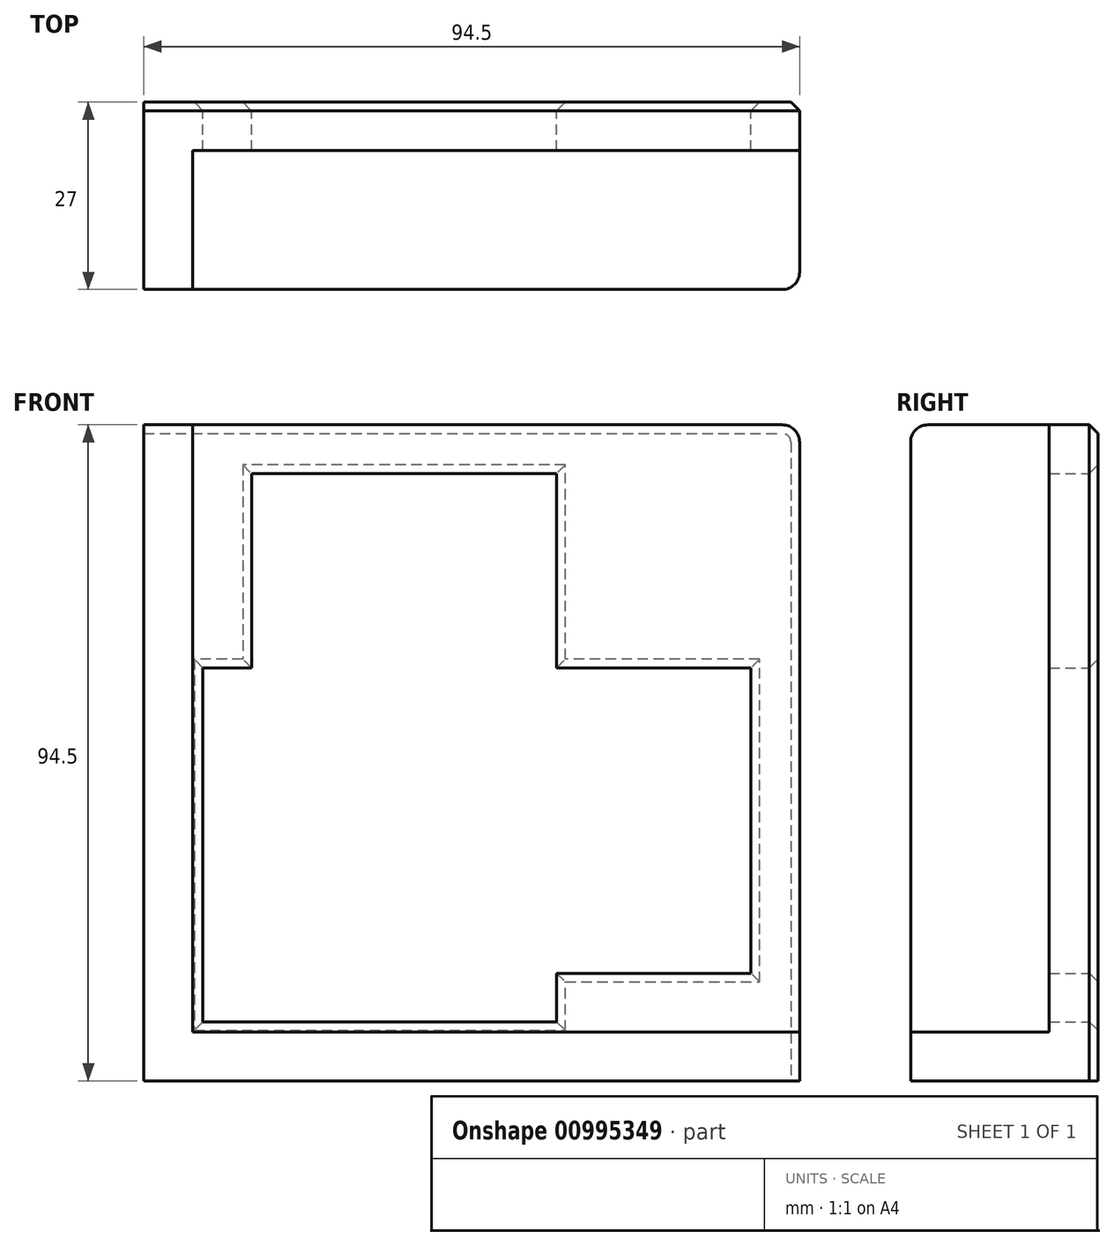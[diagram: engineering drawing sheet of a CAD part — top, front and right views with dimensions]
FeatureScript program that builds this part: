
annotation { "Feature Type Name" : "Feature", "Feature Type Description" : "" }
export const myFeature = defineFeature(function(context is Context, id is Id, definition is map)
    precondition{}
    {
        {
            var Q0;
            Q0=qCreatedBy(makeId("Front.planeOp"),FACE);
            var sketch = newSketch(context, id + "F0", { "sketchPlane" : qUnion([Q0])});
            skLineSegment(sketch, "E0.bottom", {"start": v(-22.62, 25.2) * mm, "end": v(29.88, 25.2) * mm});
            skLineSegment(sketch, "E0.top", {"start": v(-22.62, -27.3) * mm, "end": v(29.88, -27.3) * mm});
            skLineSegment(sketch, "E0.left", {"start": v(-22.62, 25.2) * mm, "end": v(-22.62, -27.3) * mm});
            skLineSegment(sketch, "E0.right", {"start": v(29.88, 25.2) * mm, "end": v(29.88, -27.3) * mm});
            skLineSegment(sketch, "E1.bottom", {"start": v(-22.62, 25.2) * mm, "end": v(-29.62, 25.2) * mm});
            skLineSegment(sketch, "E1.top", {"start": v(-22.62, -27.3) * mm, "end": v(-29.62, -27.3) * mm});
            skLineSegment(sketch, "E1.right", {"start": v(-29.62, 25.2) * mm, "end": v(-29.62, -27.3) * mm});
            skLineSegment(sketch, "E2.bottom", {"start": v(-29.62, -27.3) * mm, "end": v(-22.62, -27.3) * mm});
            skLineSegment(sketch, "E2.top", {"start": v(-29.62, -34.3) * mm, "end": v(-22.62, -34.3) * mm});
            skLineSegment(sketch, "E2.left", {"start": v(-29.62, -27.3) * mm, "end": v(-29.62, -34.3) * mm});
            skLineSegment(sketch, "E2.right", {"start": v(-22.62, -27.3) * mm, "end": v(-22.62, -34.3) * mm});
            skLineSegment(sketch, "E3.bottom", {"start": v(-22.62, -34.3) * mm, "end": v(29.88, -34.3) * mm});
            skLineSegment(sketch, "E3.left", {"start": v(-22.62, -34.3) * mm, "end": v(-22.62, -27.3) * mm});
            skLineSegment(sketch, "E3.right", {"start": v(29.88, -34.3) * mm, "end": v(29.88, -27.3) * mm});
            skLineSegment(sketch, "E4.bottom", {"start": v(29.88, 25.2) * mm, "end": v(64.88, 25.2) * mm});
            skLineSegment(sketch, "E4.top", {"start": v(29.88, -27.3) * mm, "end": v(64.88, -27.3) * mm});
            skLineSegment(sketch, "E4.right", {"start": v(64.88, 25.2) * mm, "end": v(64.88, -27.3) * mm});
            skLineSegment(sketch, "E5.bottom", {"start": v(29.88, 25.2) * mm, "end": v(-22.62, 25.2) * mm});
            skLineSegment(sketch, "E5.top", {"start": v(29.88, 60.2) * mm, "end": v(-22.62, 60.2) * mm});
            skLineSegment(sketch, "E5.left", {"start": v(29.88, 25.2) * mm, "end": v(29.88, 60.2) * mm});
            skLineSegment(sketch, "E5.right", {"start": v(-22.62, 25.2) * mm, "end": v(-22.62, 60.2) * mm});
            skLineSegment(sketch, "E6.top", {"start": v(29.88, 60.2) * mm, "end": v(64.88, 60.2) * mm});
            skLineSegment(sketch, "E6.right", {"start": v(64.88, 25.2) * mm, "end": v(64.88, 60.2) * mm});
            skLineSegment(sketch, "E7.bottom", {"start": v(29.88, 25.2) * mm, "end": v(57.88, 25.2) * mm});
            skLineSegment(sketch, "E7.top", {"start": v(29.88, -18.8) * mm, "end": v(57.88, -18.8) * mm});
            skLineSegment(sketch, "E7.left", {"start": v(29.88, 25.2) * mm, "end": v(29.88, -18.8) * mm});
            skLineSegment(sketch, "E7.right", {"start": v(57.88, 25.2) * mm, "end": v(57.88, -18.8) * mm});
            skLineSegment(sketch, "E8.bottom", {"start": v(29.88, 25.2) * mm, "end": v(-14.12, 25.2) * mm});
            skLineSegment(sketch, "E8.top", {"start": v(29.88, 53.2) * mm, "end": v(-14.12, 53.2) * mm});
            skLineSegment(sketch, "E8.left", {"start": v(29.88, 25.2) * mm, "end": v(29.88, 53.2) * mm});
            skLineSegment(sketch, "E8.right", {"start": v(-14.12, 25.2) * mm, "end": v(-14.12, 53.2) * mm});
            skLineSegment(sketch, "E9.bottom", {"start": v(64.88, -27.3) * mm, "end": v(29.88, -27.3) * mm});
            skLineSegment(sketch, "E9.top", {"start": v(64.88, -34.3) * mm, "end": v(29.88, -34.3) * mm});
            skLineSegment(sketch, "E9.left", {"start": v(64.88, -27.3) * mm, "end": v(64.88, -34.3) * mm});
            skLineSegment(sketch, "E9.right", {"start": v(29.88, -27.3) * mm, "end": v(29.88, -34.3) * mm});
            skLineSegment(sketch, "E10.bottom", {"start": v(-29.62, 25.2) * mm, "end": v(-22.62, 25.2) * mm});
            skLineSegment(sketch, "E10.top", {"start": v(-29.62, 60.2) * mm, "end": v(-22.62, 60.2) * mm});
            skLineSegment(sketch, "E10.left", {"start": v(-29.62, 25.2) * mm, "end": v(-29.62, 60.2) * mm});
            skLineSegment(sketch, "E11.bottom", {"start": v(-22.62, 25.2) * mm, "end": v(-21.12, 25.2) * mm});
            skLineSegment(sketch, "E11.top", {"start": v(-22.62, -27.3) * mm, "end": v(-21.12, -27.3) * mm});
            skLineSegment(sketch, "E11.right", {"start": v(-21.12, 25.2) * mm, "end": v(-21.12, -27.3) * mm});
            skLineSegment(sketch, "E12.bottom", {"start": v(29.88, -25.8) * mm, "end": v(-21.12, -25.8) * mm});
            skLineSegment(sketch, "E12.top", {"start": v(29.88, -27.3) * mm, "end": v(-21.12, -27.3) * mm});
            skLineSegment(sketch, "E12.left", {"start": v(29.88, -25.8) * mm, "end": v(29.88, -27.3) * mm});
            skLineSegment(sketch, "E12.right", {"start": v(-21.12, -25.8) * mm, "end": v(-21.12, -27.3) * mm});
            skSolve(sketch);
        }
        {
            var Q0;
            Q0=makeQuery(id+"F0.imprint","IMPRINT",FACE,{"disambiguationData":[TD([[makeQuery(id+"F0.imprint","IMPRINT",EDGE,{"derivedFrom":sQuery(id+"F0.wireOp",EDGE,"E1.top")}),1.0]])]});
            var Q1;
            Q1=makeQuery(id+"F0.imprint","IMPRINT",FACE,{"disambiguationData":[TD([[makeQuery(id+"F0.imprint","IMPRINT",EDGE,{"derivedFrom":sQuery(id+"F0.wireOp",EDGE,"E3.right")}),-1.0]])]});
            var Q2;
            Q2=makeQuery(id+"F0.imprint","IMPRINT",FACE,{"disambiguationData":[TD([[makeQuery(id+"F0.imprint","IMPRINT",EDGE,{"derivedFrom":sQuery(id+"F0.wireOp",EDGE,"E0.left")}),-1.0]])]});
            var Q3;
            {var subQ2=sQuery(id+"F0.wireOp",EDGE,"E2.right");Q3=makeQuery(id+"F0.imprint","IMPRINT",FACE,{"disambiguationData":[TD([[makeQuery(id+"F0.imprint","IMPRINT",EDGE,{"derivedFrom":subQ2}),1.0]])]});}
            var Q4;
            Q4=makeQuery(id+"F0.imprint","IMPRINT",FACE,{"disambiguationData":[TD([[makeQuery(id+"F0.imprint","IMPRINT",EDGE,{"derivedFrom":sQuery(id+"F0.wireOp",EDGE,"E0.left")}),-1.0]])]});
            var Q5;
            Q5=makeQuery(id+"F0.imprint","IMPRINT",FACE,{"disambiguationData":[TD([[makeQuery(id+"F0.imprint","IMPRINT",EDGE,{"derivedFrom":sQuery(id+"F0.wireOp",EDGE,"E1.bottom")}),-1.0]])]});
            extrude(context, id + "F1", {"entities" : qUnion([Q0, Q1, Q2, Q3, Q4, Q5]), "depth" : 20 * mm, "offsetDistance" : 25 * mm});
        }
        {
            var Q0;
            {var subQ0=sQuery(id+"F0.wireOp",EDGE,"E3.right");var subQ1=makeQuery(id+"F0.imprint","IMPRINT",EDGE,{"derivedFrom":subQ0});var subQ2=sQuery(id+"F0.wireOp",EDGE,"E4.top");var subQ3=makeQuery(id+"F0.imprint","IMPRINT",EDGE,{"derivedFrom":subQ2});var subQ4=sQuery(id+"F0.wireOp",EDGE,"E6.top");var subQ6=sQuery(id+"F0.wireOp",EDGE,"E5.top");var subQ19=sQuery(id+"F0.wireOp",EDGE,"E1.top");var subQ20=makeQuery(id+"F0.imprint","IMPRINT",EDGE,{"derivedFrom":subQ19});var subQ21=sQuery(id+"F0.wireOp",EDGE,"E2.right");var subQ22=makeQuery(id+"F0.imprint","IMPRINT",EDGE,{"derivedFrom":subQ21});var subQ27=sQuery(id+"F0.wireOp",EDGE,"E0.left");var subQ28=sQuery(id+"F0.wireOp",EDGE,"E1.bottom");var subQ29=makeQuery(id+"F0.imprint","IMPRINT",EDGE,{"derivedFrom":subQ28});Q0=qUnion([makeQuery(id+"F0.imprint","IMPRINT",FACE,{"disambiguationData":[TD([[makeQuery(id+"F0.imprint","IMPRINT",EDGE,{"derivedFrom":subQ6}),1.0]])]}),makeQuery(id+"F0.imprint","IMPRINT",FACE,{"disambiguationData":[TD([[subQ22,1.0]])]}),makeQuery(id+"F0.imprint","IMPRINT",FACE,{"disambiguationData":[TD([[subQ29,-1.0]])]}),makeQuery(id+"F0.imprint","IMPRINT",FACE,{"disambiguationData":[TD([[makeQuery(id+"F0.imprint","IMPRINT",EDGE,{"derivedFrom":subQ27}),-1.0]])]}),makeQuery(id+"F0.imprint","IMPRINT",FACE,{"disambiguationData":[TD([[subQ3,1.0]])]}),makeQuery(id+"F0.imprint","IMPRINT",FACE,{"disambiguationData":[TD([[subQ20,1.0]])]}),makeQuery(id+"F0.imprint","IMPRINT",FACE,{"disambiguationData":[TD([[makeQuery(id+"F0.imprint","IMPRINT",EDGE,{"derivedFrom":subQ4}),-1.0]])]}),makeQuery(id+"F0.imprint","IMPRINT",FACE,{"disambiguationData":[TD([[subQ1,-1.0]])]})]);}
            var Q1;
            Q1=makeQuery(id+"F1.opExtrude","CAP_FACE",FACE,{"disambiguationData":[OSD([sQuery(id+"F0.wireOp",EDGE,"E0.top"),sQuery(id+"F0.wireOp",EDGE,"E0.left"),sQuery(id+"F0.wireOp",EDGE,"E1.right"),sQuery(id+"F0.wireOp",EDGE,"E2.top"),sQuery(id+"F0.wireOp",EDGE,"E2.left"),sQuery(id+"F0.wireOp",EDGE,"E3.bottom"),sQuery(id+"F0.wireOp",EDGE,"E4.top"),sQuery(id+"F0.wireOp",EDGE,"E5.right"),sQuery(id+"F0.wireOp",EDGE,"E9.top"),sQuery(id+"F0.wireOp",EDGE,"E9.left"),sQuery(id+"F0.wireOp",EDGE,"E10.top"),sQuery(id+"F0.wireOp",EDGE,"E10.left")])],"isStart":false});
            var Q2;
            {var subQ4=sQuery(id+"F0.wireOp",EDGE,"E0.left");Q2=makeQuery(id+"F0.imprint","IMPRINT",FACE,{"disambiguationData":[TD([[makeQuery(id+"F0.imprint","IMPRINT",EDGE,{"derivedFrom":subQ4}),1.0]])]});}
            var Q3;
            {var subQ5=sQuery(id+"F0.wireOp",EDGE,"E12.bottom");Q3=makeQuery(id+"F0.imprint","IMPRINT",FACE,{"disambiguationData":[TD([[makeQuery(id+"F0.imprint","IMPRINT",EDGE,{"derivedFrom":subQ5}),1.0]])]});}
            extrude(context, id + "F2", {"entities" : qUnion([Q0, Q1, Q2, Q3]), "operationType" : NewBodyOperationType.ADD, "depth" : 7 * mm, "offsetDistance" : 25 * mm});
        }
        {
            var Q0;
            Q0=makeQuery(id+"F2.opExtrude","CAP_EDGE",EDGE,{"disambiguationData":[OSD([sQuery(id+"F0.wireOp",EDGE,"E10.top")])],"isStart":false});
            var Q1;
            Q1=makeQuery(id+"F2.opExtrude","CAP_EDGE",EDGE,{"disambiguationData":[OSD([sQuery(id+"F0.wireOp",EDGE,"E9.left")])],"isStart":false});
            var Q2;
            Q2=makeQuery(id+"F2.opExtrude","SWEPT_EDGE",EDGE,{"disambiguationData":[OSD([sQuery(id+"F0.wireOp",EDGE,"E6.top"),sQuery(id+"F0.wireOp",EDGE,"E6.right")])]});
            fillet(context, id + "F3", {"entities" : qUnion([Q0, Q1, Q2]), "radius" : 2.5 * mm, "tangentPropagation" : true, "allowEdgeOverflow" : false});
        }
        {
            var Q0;
            Q0=makeQuery(id+"F2.opExtrude","CAP_EDGE",EDGE,{"disambiguationData":[OSD([sQuery(id+"F0.wireOp",EDGE,"E4.bottom")])],"isStart":true});
            var Q1;
            Q1=makeQuery(id+"F2.opExtrude","CAP_EDGE",EDGE,{"disambiguationData":[OSD([sQuery(id+"F0.wireOp",EDGE,"E7.right")])],"isStart":true});
            var Q2;
            Q2=makeQuery(id+"F2.opExtrude","CAP_EDGE",EDGE,{"disambiguationData":[OSD([sQuery(id+"F0.wireOp",EDGE,"E7.top")])],"isStart":true});
            var Q3;
            Q3=makeQuery(id+"F2.opExtrude","CAP_EDGE",EDGE,{"disambiguationData":[OSD([sQuery(id+"F0.wireOp",EDGE,"E0.right")])],"isStart":true});
            var Q4;
            Q4=makeQuery(id+"F2.opExtrude","CAP_EDGE",EDGE,{"disambiguationData":[OSD([sQuery(id+"F0.wireOp",EDGE,"E12.bottom")])],"isStart":true});
            var Q5;
            Q5=makeQuery(id+"F2.opExtrude","CAP_EDGE",EDGE,{"disambiguationData":[OSD([sQuery(id+"F0.wireOp",EDGE,"E11.right")])],"isStart":true});
            var Q6;
            Q6=makeQuery(id+"F2.opExtrude","CAP_EDGE",EDGE,{"disambiguationData":[OSD([sQuery(id+"F0.wireOp",EDGE,"E5.left")])],"isStart":true});
            var Q7;
            Q7=makeQuery(id+"F2.opExtrude","CAP_EDGE",EDGE,{"disambiguationData":[OSD([sQuery(id+"F0.wireOp",EDGE,"E8.top")])],"isStart":true});
            var Q8;
            Q8=makeQuery(id+"F2.opExtrude","CAP_EDGE",EDGE,{"disambiguationData":[OSD([sQuery(id+"F0.wireOp",EDGE,"E8.right")])],"isStart":true});
            var Q9;
            Q9=makeQuery(id+"F2.opExtrude","CAP_EDGE",EDGE,{"disambiguationData":[OSD([sQuery(id+"F0.wireOp",EDGE,"E0.bottom")])],"isStart":true});
            var Q10;
            {var subQ0=sQuery(id+"F0.wireOp",EDGE,"E9.left");Q10=makeQuery(id+"F2.boolean.opBoolean","MERGE",EDGE,{"derivedFrom":[makeQuery(id+"F1.opExtrude","CAP_EDGE",EDGE,{"disambiguationData":[OSD([subQ0])],"isStart":true}),makeQuery(id+"F2.opExtrude","CAP_EDGE",EDGE,{"disambiguationData":[OSD([sQuery(id+"F0.wireOp",EDGE,"E4.right"),sQuery(id+"F0.wireOp",EDGE,"E6.right"),subQ0])],"isStart":true})]});}
            chamfer(context, id + "F4", {"entities" : qUnion([Q0, Q1, Q2, Q3, Q4, Q5, Q6, Q7, Q8, Q9, Q10]), "width" : 1.25 * mm, "tangentPropagation" : true});
        }
    });
